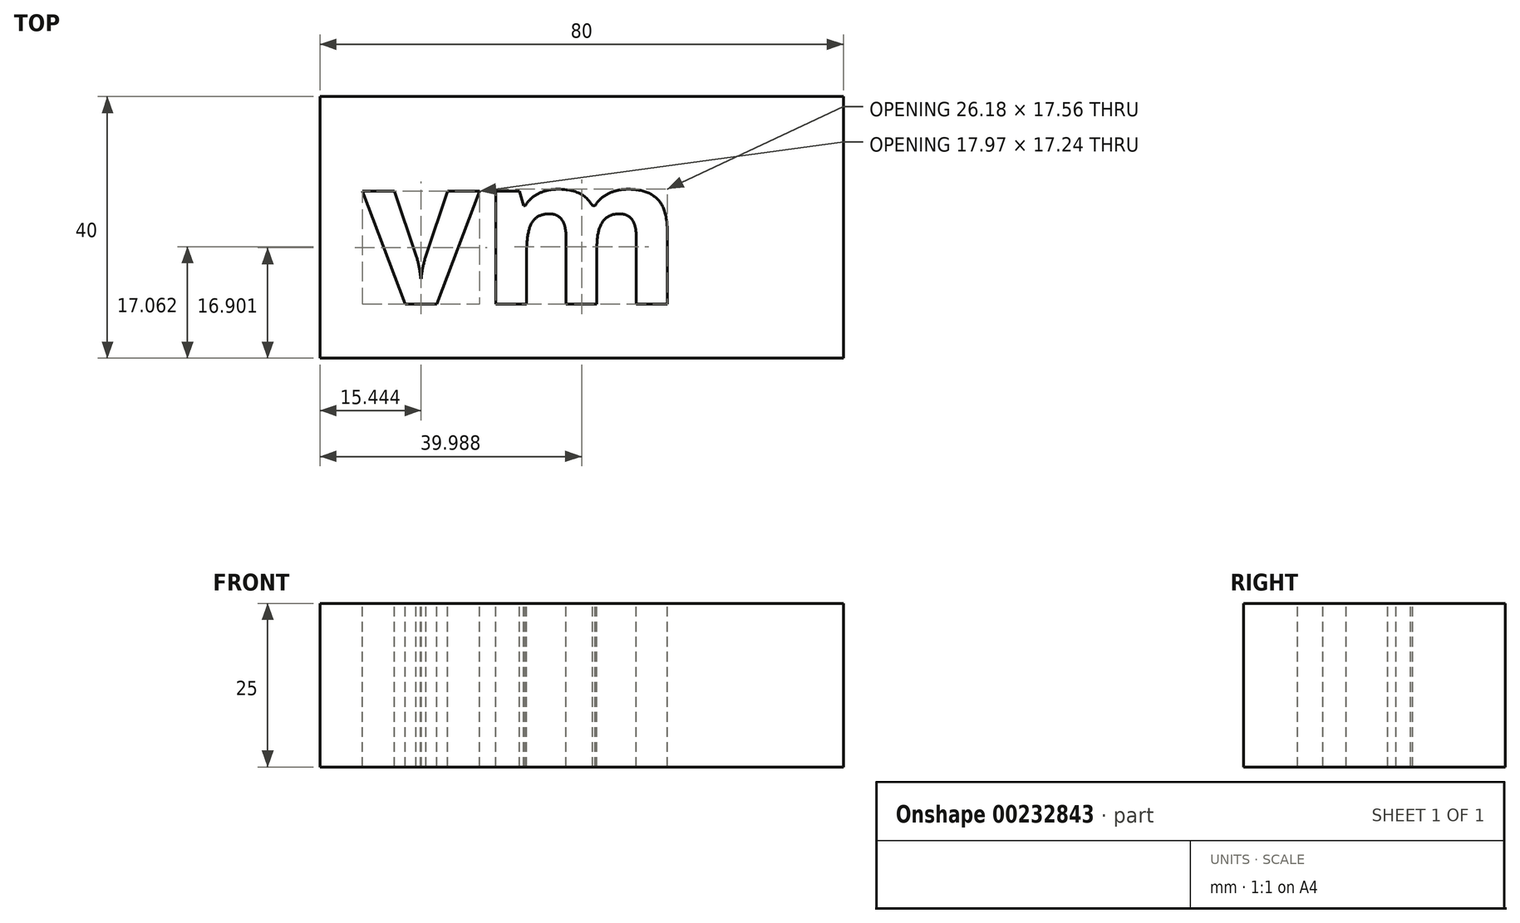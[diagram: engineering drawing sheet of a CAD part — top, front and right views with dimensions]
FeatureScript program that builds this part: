
annotation { "Feature Type Name" : "Feature", "Feature Type Description" : "" }
export const myFeature = defineFeature(function(context is Context, id is Id, definition is map)
    precondition{}
    {
        {
            var Q0;
            Q0=qCreatedBy(makeId("Top.planeOp"),FACE);
            var sketch = newSketch(context, id + "F0", { "sketchPlane" : qUnion([Q0])});
            skLineSegment(sketch, "E0.bottom", {"start": v(0, 0) * mm, "end": v(80, 0) * mm});
            skLineSegment(sketch, "E0.top", {"start": v(0, 40) * mm, "end": v(80, 40) * mm});
            skLineSegment(sketch, "E0.left", {"start": v(0, 0) * mm, "end": v(0, 40) * mm});
            skLineSegment(sketch, "E0.right", {"start": v(80, 0) * mm, "end": v(80, 40) * mm});
            skSolve(sketch);
        }
        {
            var Q0;
            Q0=makeQuery(id+"F0.imprint","IMPRINT",FACE,{"disambiguationData":[TD([[makeQuery(id+"F0.imprint","IMPRINT",EDGE,{"derivedFrom":sQuery(id+"F0.wireOp",EDGE,"E0.bottom")}),1.0]])]});
            extrude(context, id + "F1", {"entities" : qUnion([Q0]), "oppositeDirection" : true, "depth" : 25 * mm});
        }
        {
            var Q0;
            Q0=makeQuery(id+"F1.opExtrude","CAP_FACE",FACE,{"disambiguationData":[OSD([sQuery(id+"F0.wireOp",EDGE,"E0.bottom"),sQuery(id+"F0.wireOp",EDGE,"E0.top"),sQuery(id+"F0.wireOp",EDGE,"E0.left"),sQuery(id+"F0.wireOp",EDGE,"E0.right")])],"isStart":true});
            var sketch = newSketch(context, id + "F2", { "sketchPlane" : qUnion([Q0])});
            skText(sketch, "E1", { "text": "vm\n", "fontName": "OpenSans-Bold.ttf"});
            const initialGuessF2  = {"E1": [0.00646, 0.00828, 1, 0, 0.02274]};
            skSetInitialGuess(sketch, initialGuessF2);
            skSolve(sketch);
        }
        {
            var Q0;
            Q0 = qSketchRegion(id + "F2", true);
            extrude(context, id + "F3", {"entities" : qUnion([Q0]), "operationType" : NewBodyOperationType.REMOVE, "oppositeDirection" : true, "depth" : 35 * mm});
        }
    });
